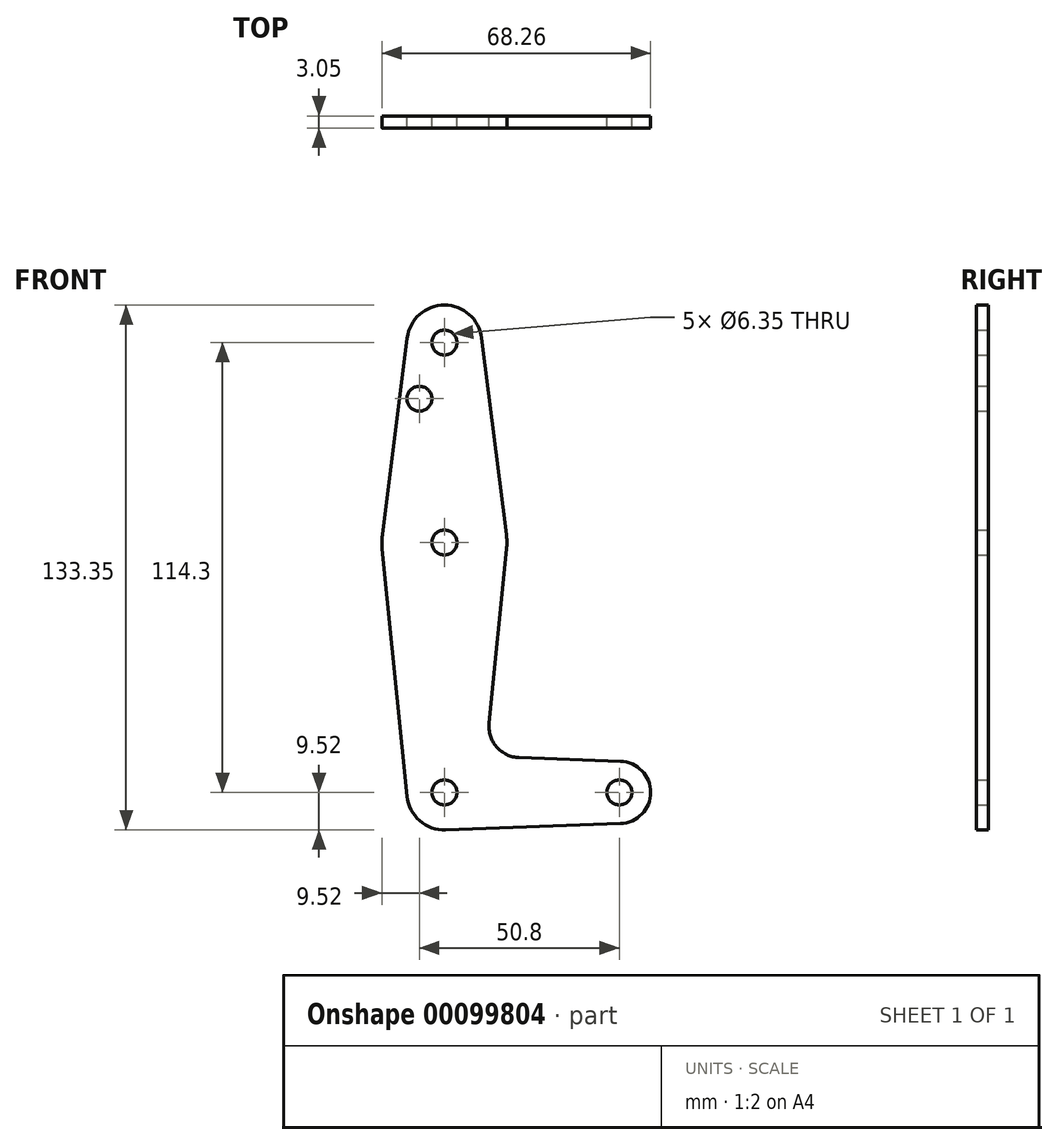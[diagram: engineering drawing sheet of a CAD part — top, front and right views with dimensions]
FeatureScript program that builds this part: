
annotation { "Feature Type Name" : "Feature", "Feature Type Description" : "" }
export const myFeature = defineFeature(function(context is Context, id is Id, definition is map)
    precondition{}
    {
        {
            var Q0;
            Q0=qCreatedBy(makeId("Front.planeOp"),FACE);
            var sketch = newSketch(context, id + "F0", { "sketchPlane" : qUnion([Q0])});
            skCircle(sketch, "E0", {"center": v(0, 0) * mm, "radius": 9.53 * mm});
            skCircle(sketch, "E1", {"center": v(44.45, 0) * mm, "radius": 7.94 * mm});
            skCircle(sketch, "E2", {"center": v(0, 63.5) * mm, "radius": 15.88 * mm});
            skCircle(sketch, "E3", {"center": v(0, 114.3) * mm, "radius": 9.53 * mm});
            skLineSegment(sketch, "E4", {"start": v(44.45, 0) * mm, "end": v(0, 0) * mm, "construction": true});
            skLineSegment(sketch, "E5", {"start": v(0, 0) * mm, "end": v(0, 63.5) * mm, "construction": true});
            skLineSegment(sketch, "E6", {"start": v(0, 63.5) * mm, "end": v(0, 114.3) * mm, "construction": true});
            skLineSegment(sketch, "E7", {"start": v(-9.45, 115.5) * mm, "end": v(-15.75, 65.48) * mm});
            skLineSegment(sketch, "E8", {"start": v(9.45, 115.5) * mm, "end": v(15.75, 65.48) * mm});
            skLineSegment(sketch, "E9", {"start": v(0.34, -9.52) * mm, "end": v(44.73, -7.93) * mm});
            skCircle(sketch, "E10", {"center": v(0, 114.3) * mm, "radius": 3.18 * mm});
            skCircle(sketch, "E11", {"center": v(0, 63.5) * mm, "radius": 3.18 * mm});
            skCircle(sketch, "E12", {"center": v(0, 0) * mm, "radius": 3.18 * mm});
            skCircle(sketch, "E13", {"center": v(44.45, 0) * mm, "radius": 3.18 * mm});
            skCircle(sketch, "E14", {"center": v(-6.35, 100.03) * mm, "radius": 3.18 * mm});
            skLineSegment(sketch, "E15", {"start": v(18.97, 8.85) * mm, "end": v(44.73, 7.93) * mm});
            skLineSegment(sketch, "E16", {"start": v(-15.8, 61.91) * mm, "end": v(-9.48, -0.95) * mm});
            skLineSegment(sketch, "E17", {"start": v(15.8, 61.91) * mm, "end": v(11.34, 17.6) * mm});
            skArc(sketch, "E18.filletArc", {"start": v(11.34, 17.6) * mm, "mid": v(13.26, 11.57) * mm, "end": v(18.97, 8.85) * mm});
            skSolve(sketch);
        }
        {
            var Q0;
            Q0 = qSketchRegion(id + "F0", true);
            extrude(context, id + "F1", {"entities" : qUnion([Q0]), "depth" : 3.05 * mm});
        }
    });
